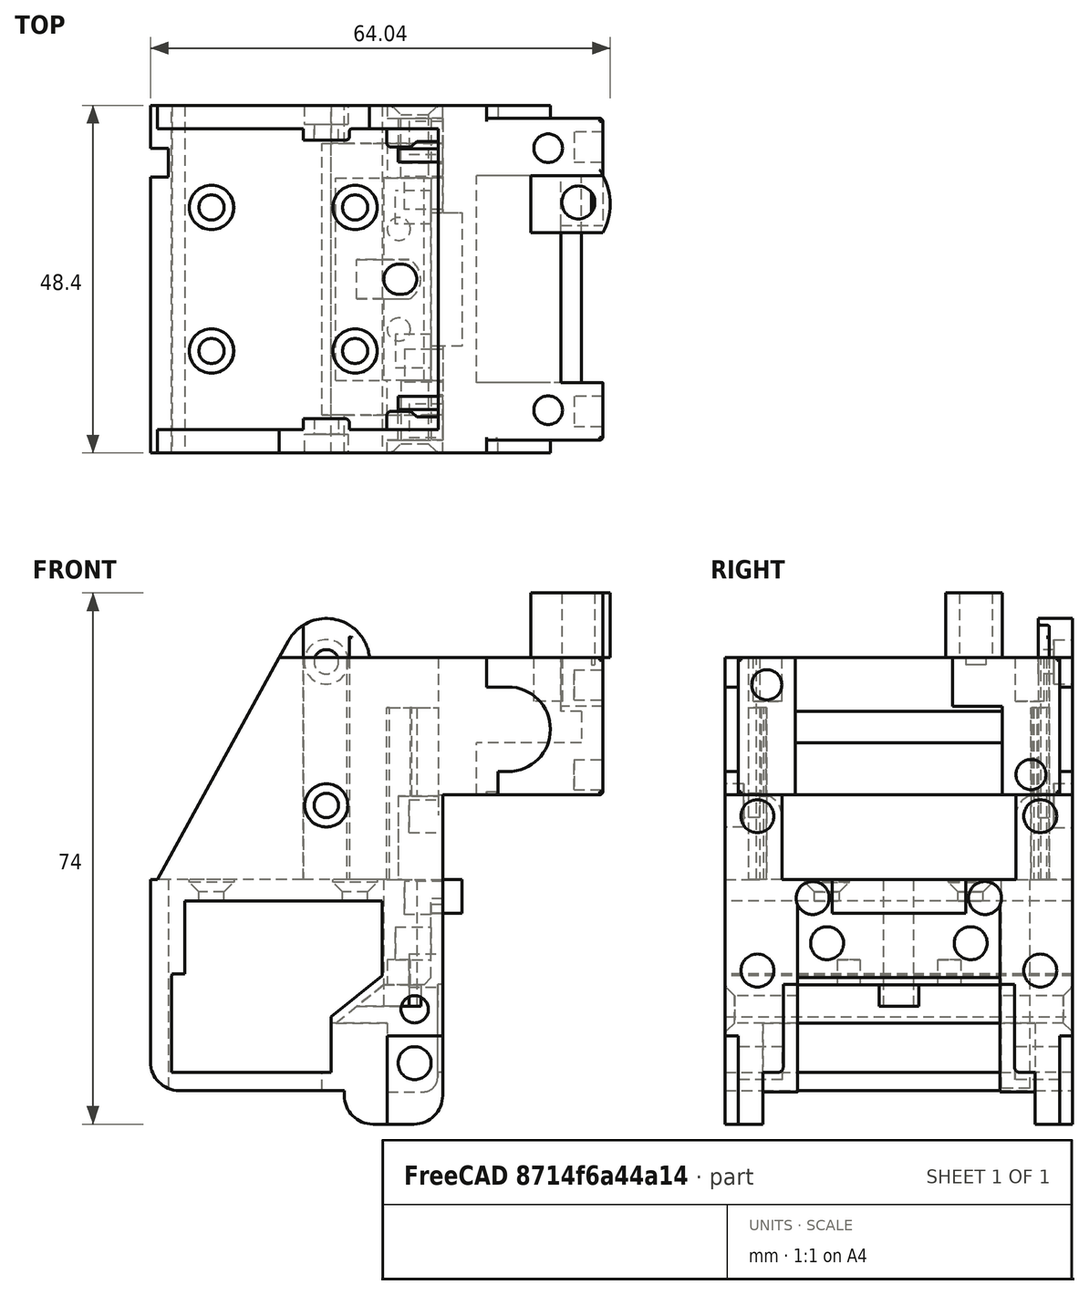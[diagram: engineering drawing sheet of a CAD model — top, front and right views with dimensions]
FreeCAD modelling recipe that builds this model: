
FCSTD DOCUMENT  (FreeCAD 1.0R38641 +468 (Git))
Label: k1_toolhead_20x10
License: All rights reserved
LicenseURL: https://en.wikipedia.org/wiki/All_rights_reserved
objects: App::Link×3, Part::Feature×1, PartDesign::FeatureBase×1, PartDesign::Body×1, App::Part×1
note: 4 computed .brp shape members not serialized (recipe doc carries the construction recipe); baked Part::Feature solids carry a one-line shape summary decoded from their .brp
EXTERNAL_REF file=cad_mgn12h_block.FCStd obj=Body
EXTERNAL_REF file=cad_hotend.FCStd obj=K1_Hotend
EXTERNAL_REF file=cad_extruder.FCStd obj=K1_extruder

FEATURE [Part::Feature] Part__Feature  label="step"
  shape: bbox 64.04 x 48.4 x 74 mm, 251 faces (baked)
FEATURE [PartDesign::FeatureBase] BaseFeature
  BaseFeature = -> Part__Feature
  Suppressed = false
FEATURE [PartDesign::Body] Body  label="k1_toolhead_20x10"
  AllowCompound = false
  BaseFeature = -> Part__Feature
  Group = -> [BaseFeature]
  Origin = -> Origin001
  Tip = -> BaseFeature
FEATURE [App::Link] Link  label="cad_mgn12_link"
  LinkPlacement = pos=(-0.49,-22.7,31.1) rot=(0.707107,0.707107,0;3.14159rad)
  LinkedObject = -> <external cad_mgn12h_block.FCStd>#Body
  Placement = pos=(-0.49,-22.7,31.1) rot=(0.707107,0.707107,0;3.14159rad)
FEATURE [App::Link] Link001  label="cad_hotend_link"
  LinkedObject = -> <external cad_hotend.FCStd>#K1_Hotend
FEATURE [App::Link] Link002  label="cad_extruder_link"
  LinkPlacement = pos=(2.30001,-0.299999,53.5) rot=(0,0,1;1.5708rad)
  LinkedObject = -> <external cad_extruder.FCStd>#K1_extruder
  Placement = pos=(2.30001,-0.299999,53.5) rot=(0,0,1;1.5708rad)
FEATURE [App::Part] Part  label="k1_toolhead_20x10_part"
  Group = -> [Body,Link,Link001,Link002]
  Origin = -> Origin

RESOLVED EXTERNAL PARTS (link-assembly join: the EXTERNAL_REF files above that resolve inside this repo's crawl, each included once):
---- part cad_mgn12h_block.FCStd = doc fcstd_671538b6926e ----
FCSTD DOCUMENT  (FreeCAD 1.0R38641 +468 (Git))
Label: cad_mgn12h_block
License: All rights reserved
LicenseURL: https://en.wikipedia.org/wiki/All_rights_reserved
objects: Sketcher::SketchObject×3, PartDesign::Pocket×2, PartDesign::Pad×1, PartDesign::Body×1
note: 16 computed .brp shape members not serialized (recipe doc carries the construction recipe); baked Part::Feature solids carry a one-line shape summary decoded from their .brp

FEATURE [Sketcher::SketchObject] Sketch
  ArcFitTolerance = 0
  AttachmentSupport = -> [YZ_Plane]
  FullyConstrained = true
  MakeInternals = false
  MapMode = 5
  Placement = pos=(0,0,0) rot=(0.57735,0.57735,0.57735;2.0944rad)
  sketch-geometry (4):
    g0: LineSegment StartX=13.5 StartY=0 StartZ=0 EndX=-13.5 EndY=-1e-16 EndZ=0
    g1: LineSegment StartX=-13.5 StartY=-1e-16 StartZ=0 EndX=-13.5 EndY=10 EndZ=0
    g2: LineSegment StartX=-13.5 StartY=10 StartZ=0 EndX=13.5 EndY=10 EndZ=0
    g3: LineSegment StartX=13.5 StartY=10 StartZ=0 EndX=13.5 EndY=0 EndZ=0
  constraints (11):
    c: Coincident(g0,g1)
    c: Coincident(g1,g2)
    c: Coincident(g2,g3)
    c: Coincident(g3,g0)
    c: Horizontal(g2)
    c: Vertical(g1)
    c: Vertical(g3)
    c: PointOnObject(g0,g-1)
    c: Symmetric(g0,g0,g-2)
    c: Distance(g2) = 27
    c: Distance(g1) = 10
FEATURE [PartDesign::Pad] Pad
  Direction = (1,0,0)
  Length = 45.4
  Length2 = 10
  Placement = pos=(0,0,0) rot=(1,1,1;2.0944rad)
  Profile = -> Sketch
  ReferenceAxis = -> Sketch [N_Axis]
  Suppressed = false
  Type = 0
FEATURE [Sketcher::SketchObject] Sketch001
  ArcFitTolerance = 0
  AttachmentSupport = -> [Pad]
  FullyConstrained = true
  MakeInternals = false
  MapMode = 5
  Placement = pos=(0,0,0) rot=(0.707107,0.707107,0;3.14159rad)
  sketch-geometry (8):
    g0: LineSegment [constr] StartX=-10 StartY=32.7 StartZ=0 EndX=10 EndY=32.7 EndZ=0
    g1: LineSegment [constr] StartX=10 StartY=32.7 StartZ=0 EndX=10 EndY=12.7 EndZ=0
    g2: LineSegment [constr] StartX=10 StartY=12.7 StartZ=0 EndX=-10 EndY=12.7 EndZ=0
    g3: LineSegment [constr] StartX=-10 StartY=12.7 StartZ=0 EndX=-10 EndY=32.7 EndZ=0
    g4: Circle CenterX=-10 CenterY=32.7 CenterZ=0 NormalX=0 NormalY=0 NormalZ=1 AngleXU=0 Radius=1.5
    g5: Circle CenterX=10 CenterY=32.7 CenterZ=0 NormalX=0 NormalY=0 NormalZ=1 AngleXU=0 Radius=1.5
    g6: Circle CenterX=10 CenterY=12.7 CenterZ=0 NormalX=0 NormalY=0 NormalZ=1 AngleXU=0 Radius=1.5
    g7: Circle CenterX=-10 CenterY=12.7 CenterZ=0 NormalX=0 NormalY=0 NormalZ=1 AngleXU=0 Radius=1.5
  constraints (19):
    c: Coincident(g0,g1)
    c: Coincident(g1,g2)
    c: Coincident(g2,g3)
    c: Coincident(g3,g0)
    c: Horizontal(g2)
    c: Vertical(g1)
    c: Vertical(g3)
    c: Symmetric(g0,g0,g-2)
    c: Distance(g0) = 20
    c: Distance(g1) = 20
    c: DistanceY(g-1,g2) = 12.7
    c: Coincident(g4,g0)
    c: Coincident(g5,g0)
    c: Coincident(g6,g1)
    c: Coincident(g7,g2)
    c: Equal(g7,g6)
    c: Equal(g6,g5)
    c: Equal(g5,g4)
    c: Radius(g4) = 1.5
FEATURE [PartDesign::Pocket] Pocket
  BaseFeature = -> Pad
  Direction = (0,0,1)
  Length = 5
  Length2 = 5
  Placement = pos=(0,0,0) rot=(1,1,1;2.0944rad)
  Profile = -> Sketch001
  ReferenceAxis = -> Sketch001 [N_Axis]
  Suppressed = false
  Type = 0
FEATURE [Sketcher::SketchObject] Sketch002
  ArcFitTolerance = 0
  AttachmentSupport = -> [Pocket]
  ExternalGeometry = -> [Pocket]
  FullyConstrained = true
  MakeInternals = false
  MapMode = 5
  Placement = pos=(0,0,0) rot=(0.57735,0.57735,-0.57735;4.18879rad)
  sketch-geometry (4):
    g0: LineSegment StartX=-6 StartY=-10 StartZ=0 EndX=6 EndY=-10 EndZ=0
    g1: LineSegment StartX=6 StartY=-10 StartZ=0 EndX=6 EndY=-5 EndZ=0
    g2: LineSegment StartX=6 StartY=-5 StartZ=0 EndX=-6 EndY=-5 EndZ=0
    g3: LineSegment StartX=-6 StartY=-5 StartZ=0 EndX=-6 EndY=-10 EndZ=0
  constraints (11):
    c: Coincident(g0,g1)
    c: Coincident(g1,g2)
    c: Coincident(g2,g3)
    c: Coincident(g3,g0)
    c: Horizontal(g0)
    c: Vertical(g1)
    c: Vertical(g3)
    c: PointOnObject(g0,g-3)
    c: Symmetric(g2,g1,g-2)
    c: Distance(g1) = 5
    c: Distance(g2) = 12
FEATURE [PartDesign::Pocket] Pocket001
  BaseFeature = -> Pocket
  Direction = (1,0,0)
  Length = 5
  Length2 = 5
  Placement = pos=(0,0,0) rot=(1,1,1;2.0944rad)
  Profile = -> Sketch002
  ReferenceAxis = -> Sketch002 [N_Axis]
  Suppressed = false
  Type = 1
FEATURE [PartDesign::Body] Body  label="mgn12h_block"
  AllowCompound = false
  Group = -> [Sketch,Pad,Sketch001,Pocket,Sketch002,Pocket001]
  Origin = -> Origin
  Placement = pos=(0,13.5,0) rot=(0,0,1;0rad)
  Tip = -> Pocket001
